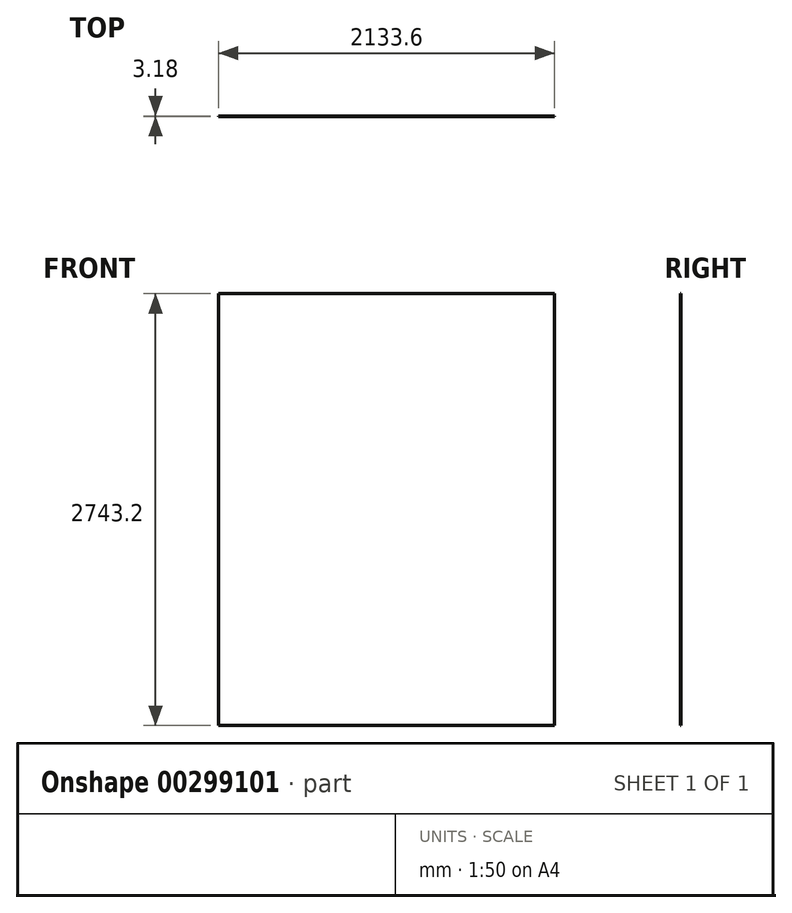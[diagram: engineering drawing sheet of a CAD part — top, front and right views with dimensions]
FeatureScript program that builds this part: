
annotation { "Feature Type Name" : "Feature", "Feature Type Description" : "" }
export const myFeature = defineFeature(function(context is Context, id is Id, definition is map)
    precondition{}
    {
        {
            var Q0;
            Q0=qCreatedBy(makeId("Front.planeOp"),FACE);
            var sketch = newSketch(context, id + "F0", { "sketchPlane" : qUnion([Q0])});
            skLineSegment(sketch, "E0.bottom", {"start": v(-1066.8, 1371.6) * mm, "end": v(1066.8, 1371.6) * mm});
            skLineSegment(sketch, "E0.top", {"start": v(-1066.8, -1371.6) * mm, "end": v(1066.8, -1371.6) * mm});
            skLineSegment(sketch, "E0.left", {"start": v(-1066.8, 1371.6) * mm, "end": v(-1066.8, -1371.6) * mm});
            skLineSegment(sketch, "E0.right", {"start": v(1066.8, 1371.6) * mm, "end": v(1066.8, -1371.6) * mm});
            skPoint(sketch, "E0.middle", {"position": v(0, 0) * mm});
            skSolve(sketch);
        }
        {
            var Q0;
            Q0 = qSketchRegion(id + "F0", true);
            extrude(context, id + "F1", {"entities" : qUnion([Q0]), "endBound" : BoundingType.SYMMETRIC, "depth" : 3.17 * mm});
        }
    });
